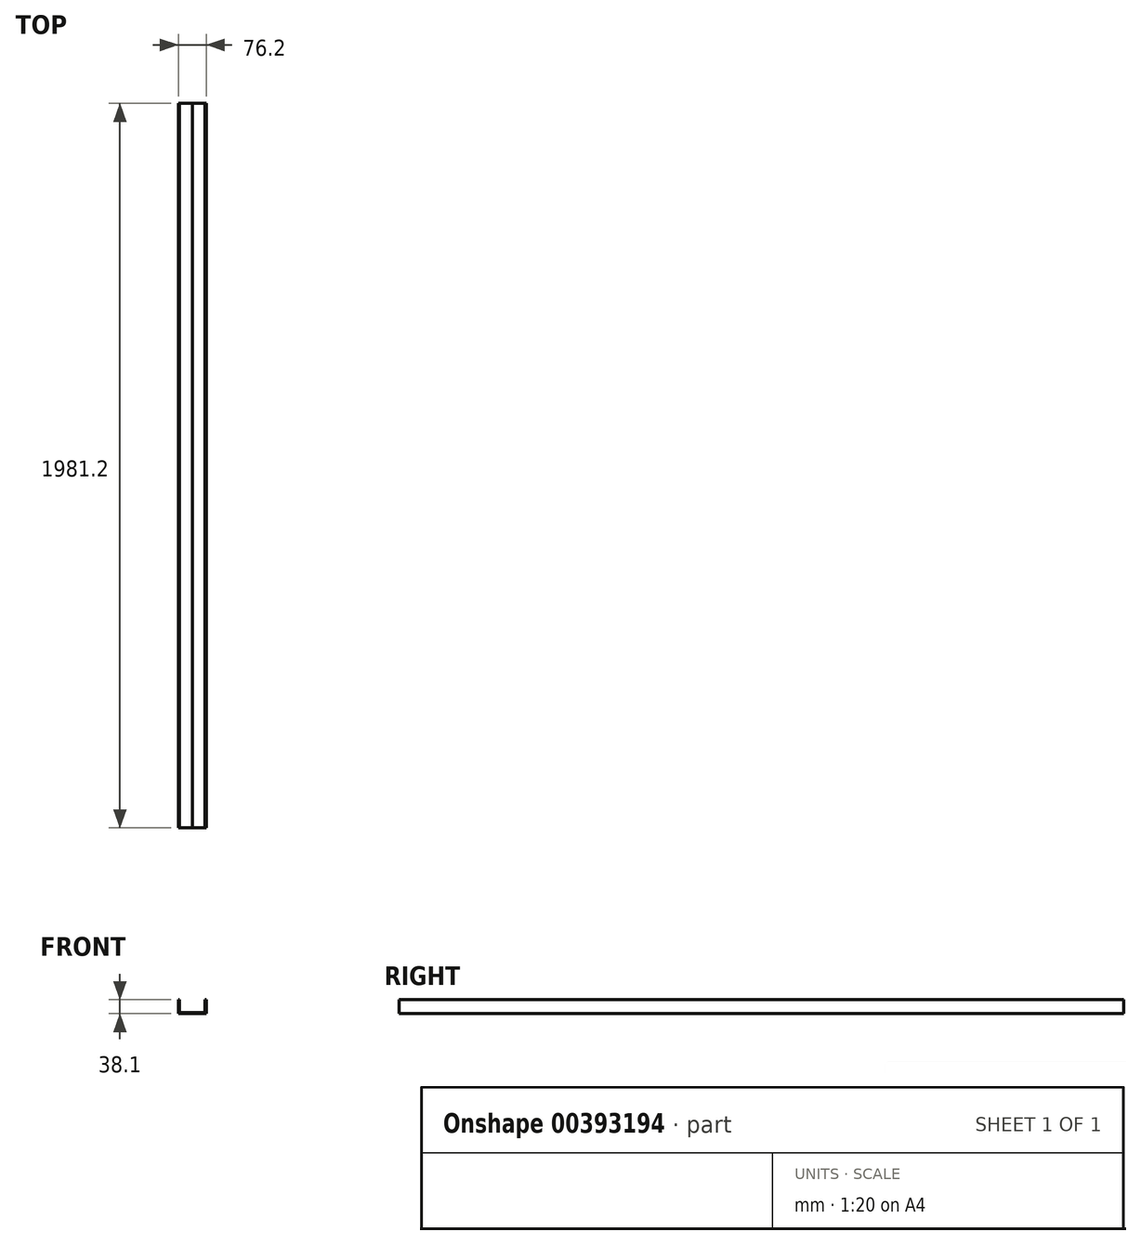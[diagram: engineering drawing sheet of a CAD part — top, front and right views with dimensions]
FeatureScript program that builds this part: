
annotation { "Feature Type Name" : "Feature", "Feature Type Description" : "" }
export const myFeature = defineFeature(function(context is Context, id is Id, definition is map)
    precondition{}
    {
        {
            var Q0;
            Q0=qCreatedBy(makeId("Front.planeOp"),FACE);
            var sketch = newSketch(context, id + "F0", { "sketchPlane" : qUnion([Q0])});
            skLineSegment(sketch, "E0", {"start": v(-101.37, 51) * mm, "end": v(-101.37, 12.9) * mm});
            skLineSegment(sketch, "E1", {"start": v(-101.37, 12.9) * mm, "end": v(-63.27, 12.9) * mm});
            skLineSegment(sketch, "E2", {"start": v(-63.27, 12.9) * mm, "end": v(-63.27, 16.08) * mm});
            skLineSegment(sketch, "E3", {"start": v(-63.27, 16.08) * mm, "end": v(-98.2, 16.08) * mm});
            skLineSegment(sketch, "E4", {"start": v(-98.2, 16.08) * mm, "end": v(-98.2, 51) * mm});
            skLineSegment(sketch, "E5", {"start": v(-98.2, 51) * mm, "end": v(-101.37, 51) * mm});
            skSolve(sketch);
        }
        {
            var Q0;
            Q0 = qSketchRegion(id + "F0", true);
            extrude(context, id + "F1", {"entities" : qUnion([Q0]), "depth" : 1981.2 * mm});
        }
        {
            var Q0;
            Q0=makeQuery(id+"F1.opExtrude","SWEPT_BODY",BODY,{"disambiguationData":[OSD([sQuery(id+"F0.wireOp",EDGE,"E0"),sQuery(id+"F0.wireOp",EDGE,"E1"),sQuery(id+"F0.wireOp",EDGE,"E2"),sQuery(id+"F0.wireOp",EDGE,"E3"),sQuery(id+"F0.wireOp",EDGE,"E4"),sQuery(id+"F0.wireOp",EDGE,"E5")])]});
            var Q1;
            Q1=makeQuery(id+"F1.opExtrude","SWEPT_FACE",FACE,{"disambiguationData":[OSD([sQuery(id+"F0.wireOp",EDGE,"E2")])]});
            mirror(context, id + "F2", {"entities" : qUnion([Q0]), "mirrorPlane" : qUnion([Q1])});
        }
    });
